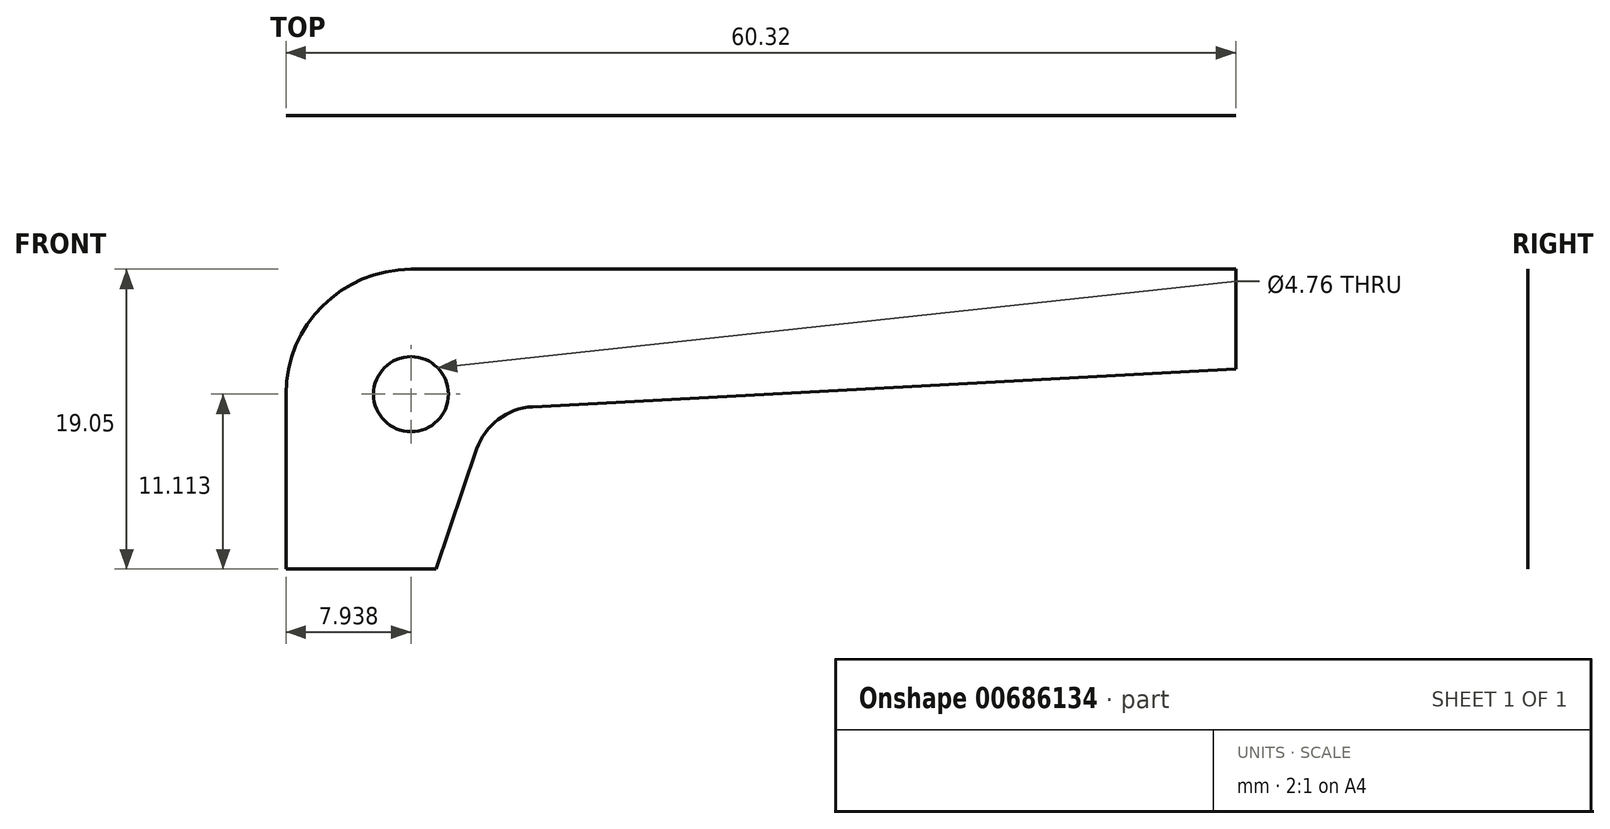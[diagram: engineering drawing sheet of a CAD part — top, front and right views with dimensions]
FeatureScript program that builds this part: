
annotation { "Feature Type Name" : "Feature", "Feature Type Description" : "" }
export const myFeature = defineFeature(function(context is Context, id is Id, definition is map)
    precondition{}
    {
        {
            var Q0;
            Q0=qCreatedBy(makeId("Front.planeOp"),FACE);
            var sketch = newSketch(context, id + "F0", { "sketchPlane" : qUnion([Q0])});
            skLineSegment(sketch, "E0.top", {"start": v(7.94, 19.05) * mm, "end": v(60.33, 19.05) * mm});
            skLineSegment(sketch, "E0.left", {"start": v(0, 0) * mm, "end": v(0, 11.11) * mm});
            skLineSegment(sketch, "E1", {"start": v(9.53, 0) * mm, "end": v(12.12, 7.63) * mm});
            skLineSegment(sketch, "E2", {"start": v(60.33, 12.7) * mm, "end": v(15.66, 10.31) * mm});
            skLineSegment(sketch, "E3", {"start": v(9.53, 0) * mm, "end": v(0, 0) * mm});
            skLineSegment(sketch, "E4", {"start": v(60.33, 12.7) * mm, "end": v(60.33, 19.05) * mm});
            skArc(sketch, "E5", {"start": v(15.66, 10.31) * mm, "mid": v(13.48, 9.51) * mm, "end": v(12.12, 7.63) * mm});
            skPoint(sketch, "E6.visualSharp", {"position": v(0, 19.05) * mm});
            skArc(sketch, "E6.filletArc", {"start": v(7.94, 19.05) * mm, "mid": v(2.32, 16.73) * mm, "end": v(0, 11.11) * mm});
            skSolve(sketch);
        }
        {
            var Q0;
            Q0 = qSketchRegion(id + "F0", true);
            extrude(context, id + "F1", {"entities" : qUnion([Q0]), "depth" : 3 / 812.8 * mm, "offsetDistance" : 25.4 * mm});
        }
        {
            var Q0;
            Q0=makeQuery(id+"F1.opExtrude","CAP_FACE",FACE,{"disambiguationData":[OSD([sQuery(id+"F0.wireOp",EDGE,"E0.top"),sQuery(id+"F0.wireOp",EDGE,"E0.left"),sQuery(id+"F0.wireOp",EDGE,"E1"),sQuery(id+"F0.wireOp",EDGE,"E2"),sQuery(id+"F0.wireOp",EDGE,"E3"),sQuery(id+"F0.wireOp",EDGE,"E4"),sQuery(id+"F0.wireOp",EDGE,"E5"),sQuery(id+"F0.wireOp",EDGE,"E6.filletArc")])],"isStart":false});
            var sketch = newSketch(context, id + "F2", { "sketchPlane" : qUnion([Q0])});
            skCircle(sketch, "E7", {"center": v(7.94, 11.11) * mm, "radius": 2.38 * mm});
            skSolve(sketch);
        }
        {
            var Q0;
            Q0=makeQuery(id+"F2.imprint","IMPRINT",FACE,{"disambiguationData":[TD([[makeQuery(id+"F2.imprint","IMPRINT",EDGE,{"derivedFrom":sQuery(id+"F2.wireOp",EDGE,"E7")}),1.0]])]});
            extrude(context, id + "F3", {"entities" : qUnion([Q0]), "operationType" : NewBodyOperationType.REMOVE, "endBound" : BoundingType.THROUGH_ALL, "oppositeDirection" : true, "depth" : 25.4 * mm, "offsetDistance" : 25.4 * mm});
        }
        {
            var Q0;
            Q0=makeQuery(id+"F1.opExtrude","SWEPT_FACE",FACE,{"disambiguationData":[OSD([sQuery(id+"F0.wireOp",EDGE,"E0.top")])]});
            var sketch = newSketch(context, id + "F4", { "sketchPlane" : qUnion([Q0])});
            skLineSegment(sketch, "E8", {"start": v(47.28, 0) * mm, "end": v(60.33, -0.8) * mm});
            skLineSegment(sketch, "E9", {"start": v(60.33, -0.8) * mm, "end": v(60.33, 0) * mm});
            skLineSegment(sketch, "E10", {"start": v(60.33, 0) * mm, "end": v(47.28, 0) * mm});
            skLineSegment(sketch, "E11.MirrorCS", {"start": v(47.28, -2.38) * mm, "end": v(60.33, -1.59) * mm});
            skLineSegment(sketch, "E12.MirrorCS", {"start": v(60.33, -2.38) * mm, "end": v(47.28, -2.38) * mm});
            skLineSegment(sketch, "E13.MirrorCS", {"start": v(60.33, -1.59) * mm, "end": v(60.33, -2.38) * mm});
            skSolve(sketch);
        }
        {
            var Q0;
            Q0=makeQuery(id+"F4.imprint","IMPRINT",FACE,{"disambiguationData":[TD([[makeQuery(id+"F4.imprint","IMPRINT",EDGE,{"derivedFrom":sQuery(id+"F4.wireOp",EDGE,"E8")}),1.0]])]});
            var Q1;
            Q1=makeQuery(id+"F4.imprint","IMPRINT",FACE,{"disambiguationData":[TD([[makeQuery(id+"F4.imprint","IMPRINT",EDGE,{"derivedFrom":sQuery(id+"F4.wireOp",EDGE,"E11.MirrorCS")}),-1.0]])]});
            extrude(context, id + "F5", {"entities" : qUnion([Q0, Q1]), "operationType" : NewBodyOperationType.REMOVE, "oppositeDirection" : true, "depth" : 25.4 * mm, "offsetDistance" : 25.4 * mm});
        }
    });
